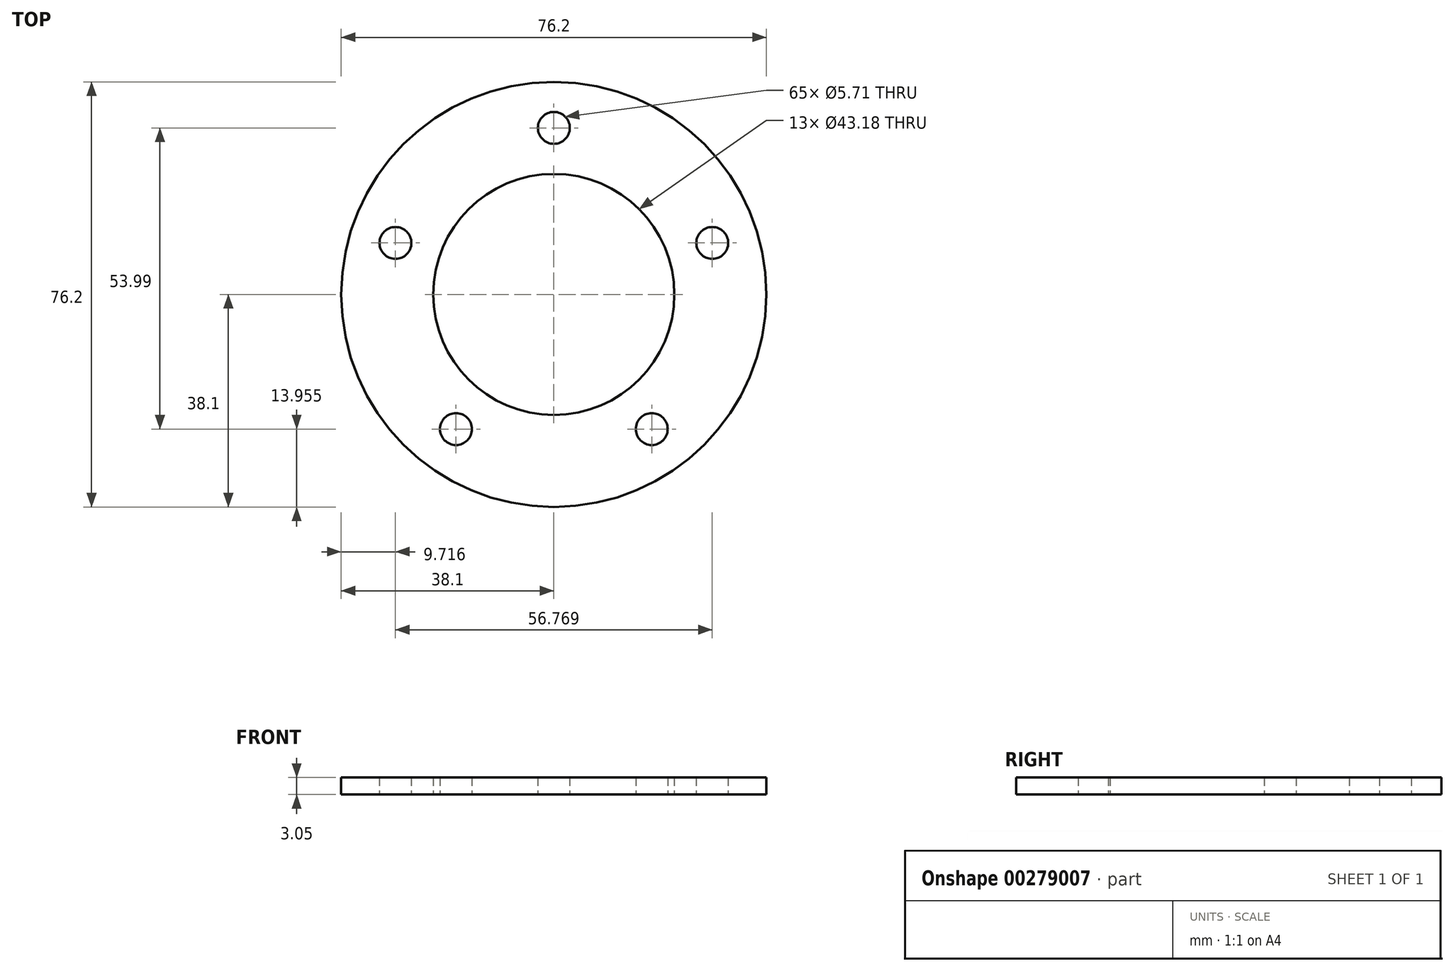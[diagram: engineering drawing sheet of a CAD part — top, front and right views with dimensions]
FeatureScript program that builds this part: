
annotation { "Feature Type Name" : "Feature", "Feature Type Description" : "" }
export const myFeature = defineFeature(function(context is Context, id is Id, definition is map)
    precondition{}
    {
        {
            var Q0;
            Q0=qCreatedBy(makeId("Top.planeOp"),FACE);
            var sketch = newSketch(context, id + "F0", { "sketchPlane" : qUnion([Q0])});
            skCircle(sketch, "E0", {"center": v(0, 0) * mm, "radius": 38.1 * mm});
            skCircle(sketch, "E1", {"center": v(0, 0) * mm, "radius": 21.59 * mm});
            skCircle(sketch, "E2", {"center": v(0, 0) * mm, "radius": 29.85 * mm, "construction": true});
            skLineSegment(sketch, "E3", {"start": v(0, 38.1) * mm, "end": v(0, 21.59) * mm, "construction": true});
            skPoint(sketch, "E4", {"position": v(0, 29.85) * mm});
            skCircle(sketch, "E5", {"center": v(0, 29.85) * mm, "radius": 2.86 * mm});
            skCircle(sketch, "E6.1.0", {"center": v(-28.38, 9.22) * mm, "radius": 2.86 * mm});
            skCircle(sketch, "E6.1.1", {"center": v(0, 0) * mm, "radius": 29.84 * mm, "construction": true});
            skCircle(sketch, "E6.2.0", {"center": v(-17.54, -24.15) * mm, "radius": 2.86 * mm});
            skCircle(sketch, "E7.1.3.0", {"center": v(17.54, -24.15) * mm, "radius": 2.86 * mm});
            skCircle(sketch, "E7.1.4.0", {"center": v(28.38, 9.22) * mm, "radius": 2.86 * mm});
            skSolve(sketch);
        }
        {
            var Q0;
            Q0 = qSketchRegion(id + "F0", true);
            extrude(context, id + "F1", {"entities" : qUnion([Q0]), "depth" : 3.05 * mm});
        }
    });
